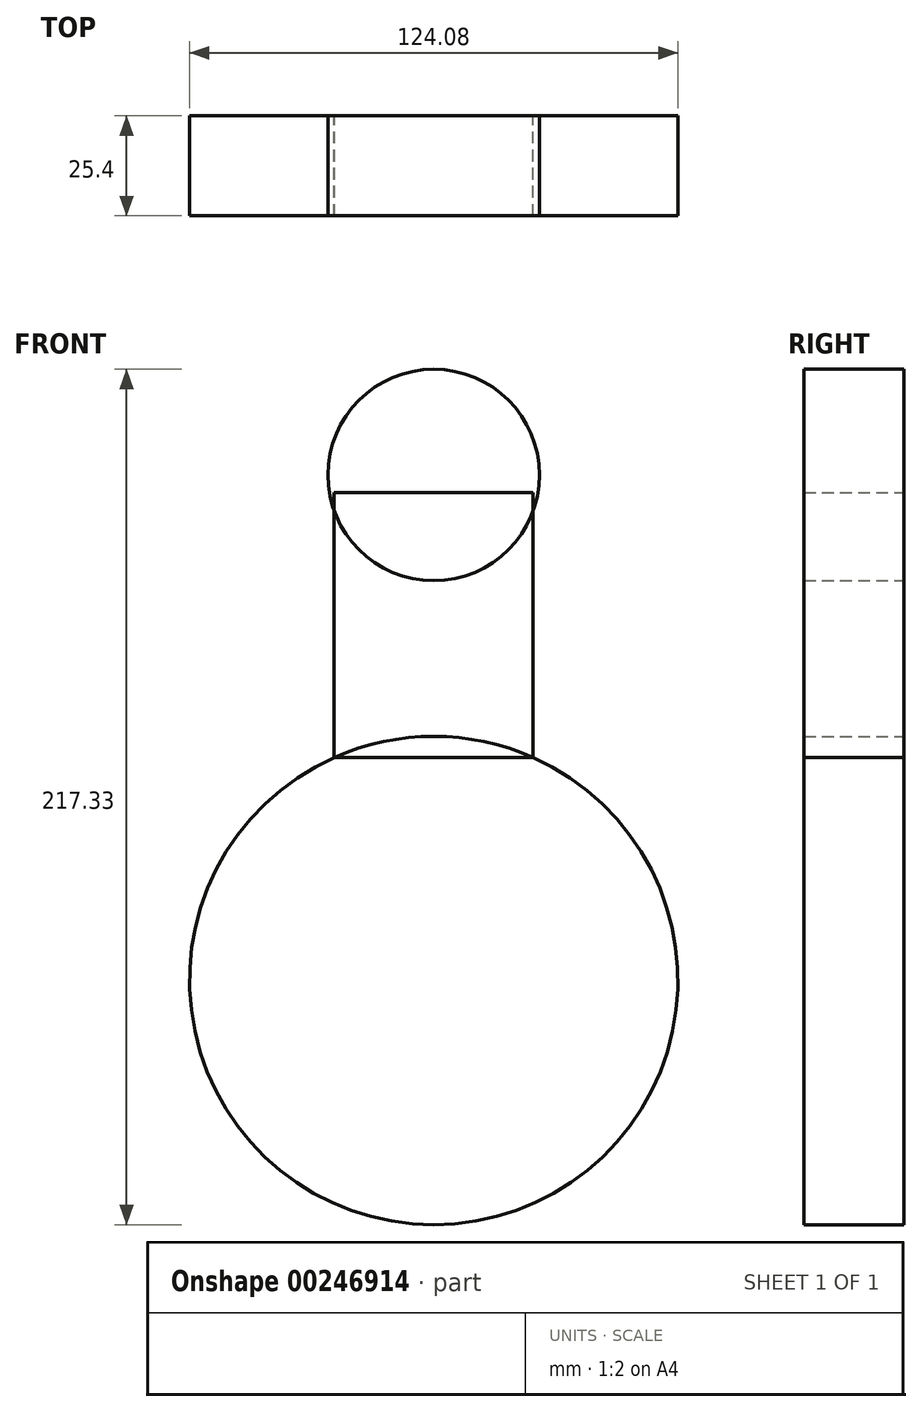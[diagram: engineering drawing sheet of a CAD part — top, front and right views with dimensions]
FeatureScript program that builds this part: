
annotation { "Feature Type Name" : "Feature", "Feature Type Description" : "" }
export const myFeature = defineFeature(function(context is Context, id is Id, definition is map)
    precondition{}
    {
        {
            var Q0;
            Q0=qCreatedBy(makeId("Front.planeOp"),FACE);
            var sketch = newSketch(context, id + "F0", { "sketchPlane" : qUnion([Q0])});
            skCircle(sketch, "E0", {"center": v(0, 0) * mm, "radius": 62.04 * mm});
            skLineSegment(sketch, "E1.bottom", {"start": v(25.17, 56.7) * mm, "end": v(-25.3, 56.7) * mm});
            skLineSegment(sketch, "E1.top", {"start": v(25.17, 123.92) * mm, "end": v(-25.3, 123.92) * mm});
            skLineSegment(sketch, "E1.left", {"start": v(25.17, 56.7) * mm, "end": v(25.17, 123.92) * mm});
            skLineSegment(sketch, "E1.right", {"start": v(-25.3, 56.7) * mm, "end": v(-25.3, 123.92) * mm});
            skSolve(sketch);
        }
        {
            var Q0;
            Q0=qCreatedBy(makeId("Front.planeOp"),FACE);
            var sketch = newSketch(context, id + "F1", { "sketchPlane" : qUnion([Q0])});
            skCircle(sketch, "E2", {"center": v(0, 128.43) * mm, "radius": 26.86 * mm});
            skSolve(sketch);
        }
        {
            var Q0;
            {var subQ0=sQuery(id+"F0.wireOp",EDGE,"E1.bottom");var subQ1=sQuery(id+"F0.wireOp",EDGE,"E0");var subQ3=makeQuery(id+"F0.imprint","INTERSECT",VERTEX,{"derivedFrom":[subQ1,subQ0]});Q0=makeQuery(id+"F0.imprint","IMPRINT",FACE,{"disambiguationData":[TD([[makeQuery(id+"F0.imprint","IMPRINT",EDGE,{"disambiguationData":[TD([[subQ3,-1.0]])],"derivedFrom":subQ1}),1.0]])]});}
            var Q1;
            Q1=makeQuery(id+"F1.imprint","IMPRINT",FACE,{"disambiguationData":[TD([[makeQuery(id+"F1.imprint","IMPRINT",EDGE,{"derivedFrom":sQuery(id+"F1.wireOp",EDGE,"E2")}),1.0]])]});
            var Q2;
            Q2=makeQuery(id+"F0.imprint","IMPRINT",FACE,{"disambiguationData":[TD([[makeQuery(id+"F0.imprint","IMPRINT",EDGE,{"derivedFrom":sQuery(id+"F0.wireOp",EDGE,"E1.top")}),1.0]])]});
            extrude(context, id + "F3", {"entities" : qUnion([Q0, Q1, Q2]), "depth" : 25.4 * mm});
        }
    });
